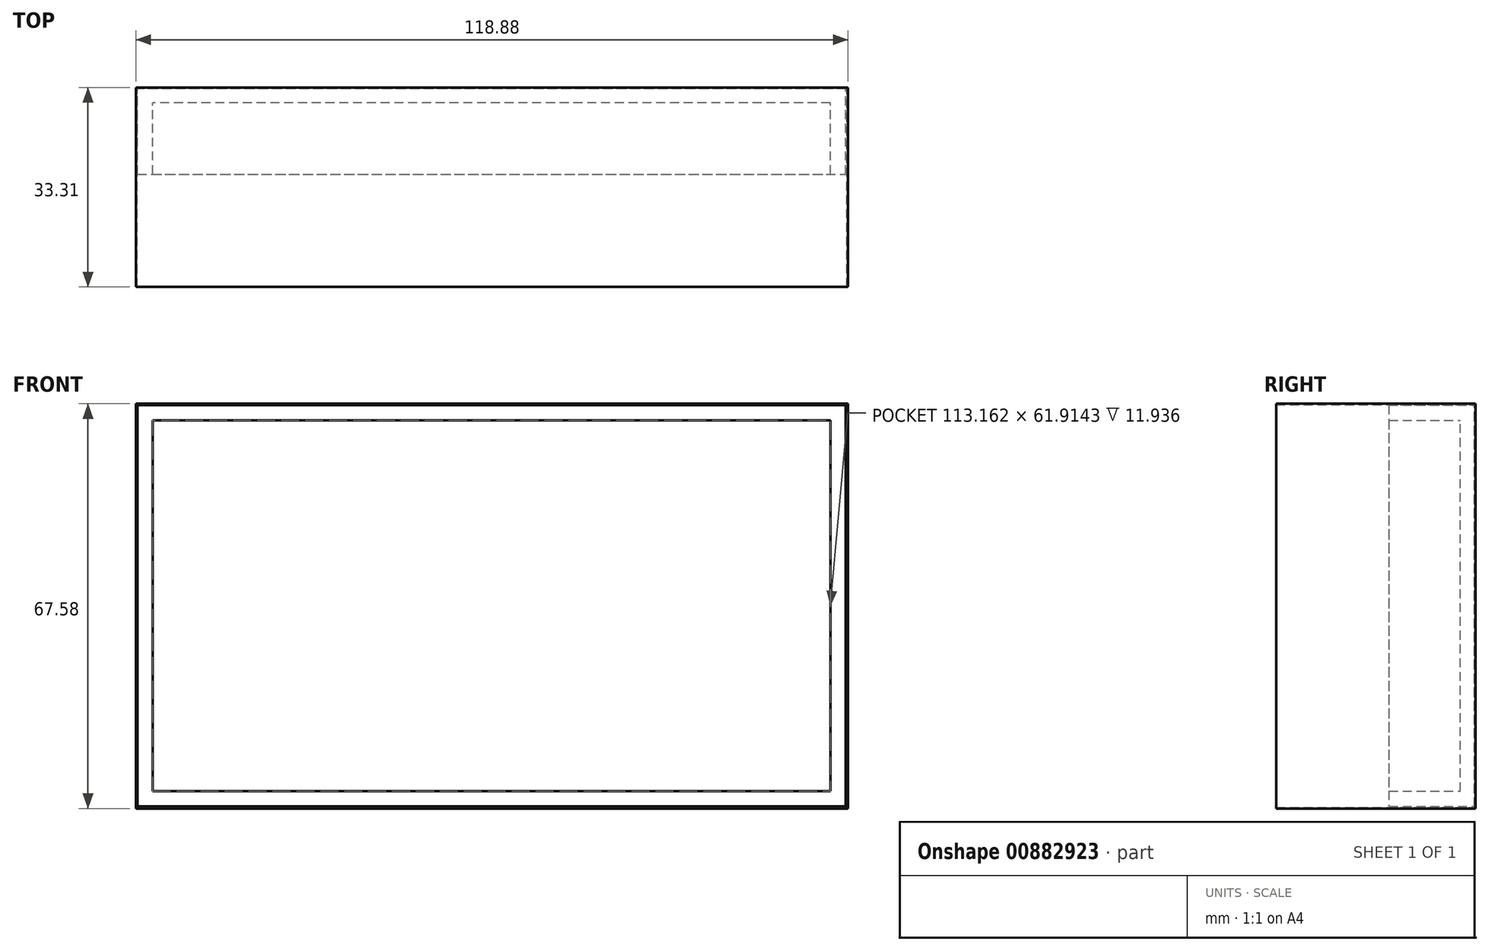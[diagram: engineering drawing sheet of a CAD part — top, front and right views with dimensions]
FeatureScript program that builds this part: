
annotation { "Feature Type Name" : "Feature", "Feature Type Description" : "" }
export const myFeature = defineFeature(function(context is Context, id is Id, definition is map)
    precondition{}
    {
        {
            var Q0;
            Q0=qCreatedBy(makeId("Front.planeOp"),FACE);
            var sketch = newSketch(context, id + "F0", { "sketchPlane" : qUnion([Q0])});
            skLineSegment(sketch, "E0.bottom", {"start": v(59.44, -33.8) * mm, "end": v(-59.44, -33.8) * mm});
            skLineSegment(sketch, "E0.top", {"start": v(59.44, 33.8) * mm, "end": v(-59.44, 33.8) * mm});
            skLineSegment(sketch, "E0.left", {"start": v(59.44, -33.8) * mm, "end": v(59.44, 33.8) * mm});
            skLineSegment(sketch, "E0.right", {"start": v(-59.44, -33.8) * mm, "end": v(-59.44, 33.8) * mm});
            skPoint(sketch, "E0.middle", {"position": v(0, 0) * mm});
            skSolve(sketch);
        }
        {
            var Q0;
            Q0 = qSketchRegion(id + "F0", true);
            extrude(context, id + "F1", {"entities" : qUnion([Q0]), "depth" : 33.3 * mm, "offsetDistance" : 25.4 * mm});
        }
        {
            var Q0;
            Q0=makeQuery(id+"F1.opExtrude","CAP_FACE",FACE,{"disambiguationData":[OSD([sQuery(id+"F0.wireOp",EDGE,"E0.bottom"),sQuery(id+"F0.wireOp",EDGE,"E0.top"),sQuery(id+"F0.wireOp",EDGE,"E0.left"),sQuery(id+"F0.wireOp",EDGE,"E0.right")])],"isStart":false});
            shell(context, id + "F2", {"entities" : qUnion([Q0]), "thickness" : 0.2 * mm});
        }
        {
            var Q0;
            Q0=qCreatedBy(makeId("Front.planeOp"),FACE);
            var sketch = newSketch(context, id + "F3", { "sketchPlane" : qUnion([Q0])});
            skLineSegment(sketch, "E1.bottom", {"start": v(-59.2, 33.55) * mm, "end": v(59.05, 33.55) * mm});
            skLineSegment(sketch, "E1.top", {"start": v(-59.2, -33.44) * mm, "end": v(59.05, -33.44) * mm});
            skLineSegment(sketch, "E1.left", {"start": v(-59.2, 33.55) * mm, "end": v(-59.2, -33.44) * mm});
            skLineSegment(sketch, "E1.right", {"start": v(59.05, 33.55) * mm, "end": v(59.05, -33.44) * mm});
            skSolve(sketch);
        }
        {
            var Q0;
            Q0 = qSketchRegion(id + "F3", true);
            extrude(context, id + "F4", {"entities" : qUnion([Q0]), "operationType" : NewBodyOperationType.ADD, "depth" : 14.48 * mm, "offsetDistance" : 25.4 * mm});
        }
        {
            var Q0;
            Q0=makeQuery(id+"F2.opShell","OFFSET_FACE",FACE,{"disambiguationData":[OSD([sQuery(id+"F0.wireOp",EDGE,"E0.top")])]});
            var Q1;
            Q1=makeQuery(id+"F4.opExtrude","CAP_FACE",FACE,{"disambiguationData":[OSD([sQuery(id+"F3.wireOp",EDGE,"E1.bottom"),sQuery(id+"F3.wireOp",EDGE,"E1.top"),sQuery(id+"F3.wireOp",EDGE,"E1.left"),sQuery(id+"F3.wireOp",EDGE,"E1.right")])],"isStart":false});
            shell(context, id + "F5", {"entities" : qUnion([Q0, Q1]), "thickness" : 2.54 * mm});
        }
    });
